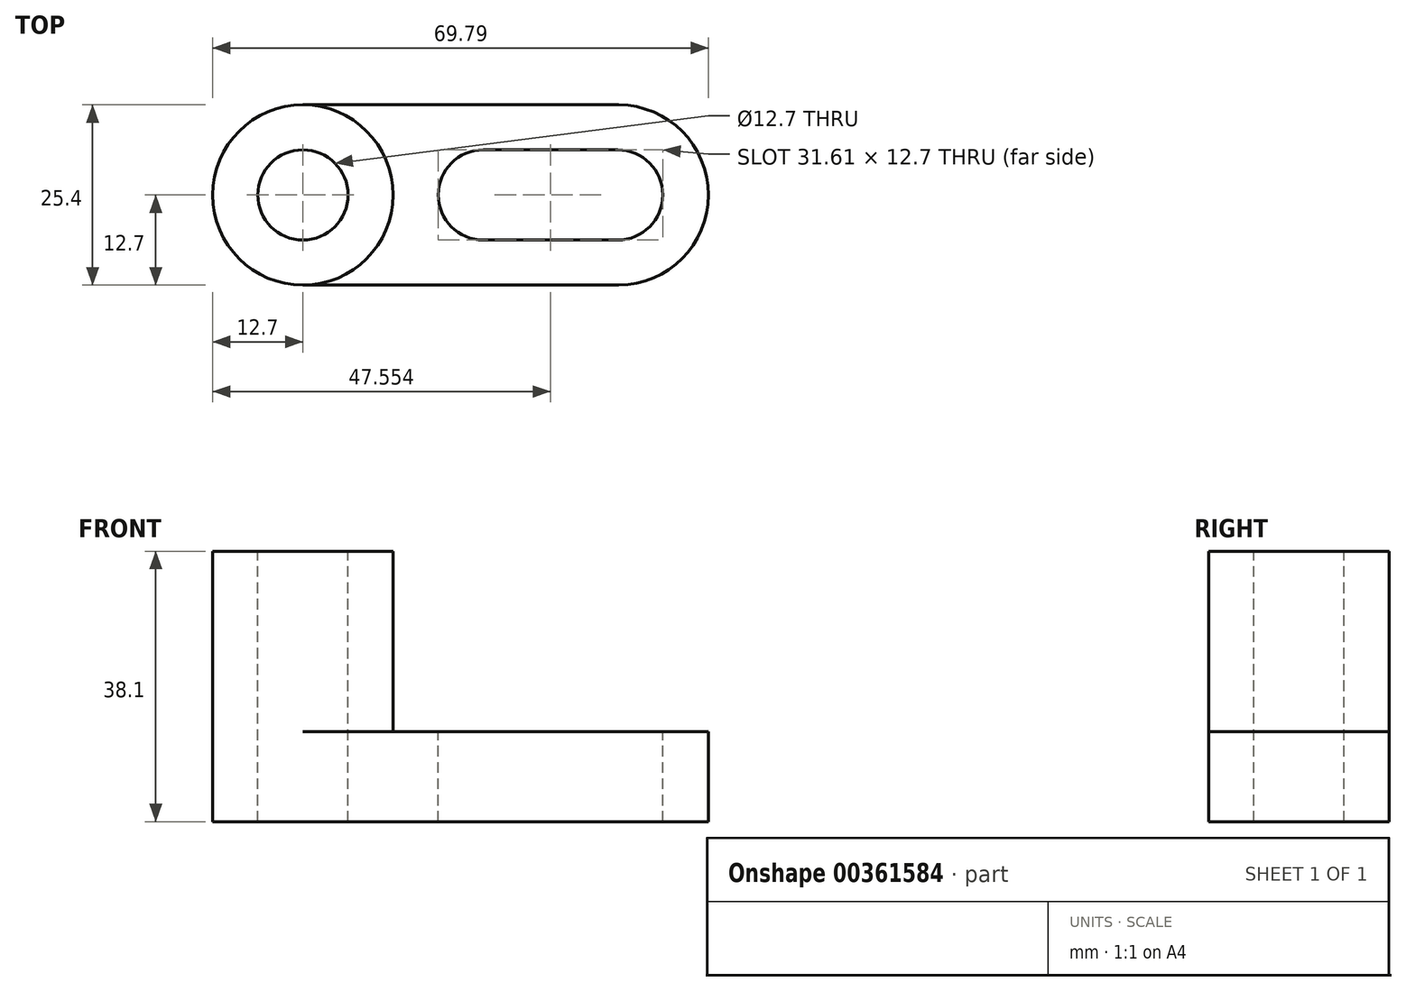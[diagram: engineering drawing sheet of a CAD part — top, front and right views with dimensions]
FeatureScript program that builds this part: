
annotation { "Feature Type Name" : "Feature", "Feature Type Description" : "" }
export const myFeature = defineFeature(function(context is Context, id is Id, definition is map)
    precondition{}
    {
        {
            var Q0;
            Q0=qCreatedBy(makeId("Front.planeOp"),FACE);
            var sketch = newSketch(context, id + "F0", { "sketchPlane" : qUnion([Q0])});
            skLineSegment(sketch, "E0", {"start": v(0, 0) * mm, "end": v(69.85, 0) * mm});
            skLineSegment(sketch, "E1", {"start": v(69.85, 0) * mm, "end": v(69.85, 12.7) * mm});
            skLineSegment(sketch, "E2", {"start": v(69.85, 12.7) * mm, "end": v(25.4, 12.7) * mm});
            skLineSegment(sketch, "E3", {"start": v(25.4, 12.7) * mm, "end": v(25.4, 38.1) * mm});
            skLineSegment(sketch, "E4", {"start": v(25.4, 38.1) * mm, "end": v(0, 38.1) * mm});
            skLineSegment(sketch, "E5", {"start": v(0, 38.1) * mm, "end": v(0, 0) * mm});
            skSolve(sketch);
        }
        {
            var Q0;
            Q0=makeQuery(id+"F0.imprint","IMPRINT",FACE,{"disambiguationData":[TD([[makeQuery(id+"F0.imprint","IMPRINT",EDGE,{"derivedFrom":sQuery(id+"F0.wireOp",EDGE,"E0")}),1.0]])]});
            extrude(context, id + "F1", {"entities" : qUnion([Q0]), "depth" : 25.4 * mm});
        }
        {
            var Q0;
            Q0=makeQuery(id+"F1.opExtrude","SWEPT_FACE",FACE,{"disambiguationData":[OSD([sQuery(id+"F0.wireOp",EDGE,"E4")])]});
            var sketch = newSketch(context, id + "F2", { "sketchPlane" : qUnion([Q0])});
            skCircle(sketch, "E6", {"center": v(12.7, -12.7) * mm, "radius": 12.7 * mm});
            skPoint(sketch, "E6.centerSnap0", {"position": v(25.4, -12.7) * mm});
            skSolve(sketch);
        }
        {
            var Q0;
            {var subQ0=sQuery(id+"F2.wireOp",EDGE,"E6");var subQ1=sQuery(id+"F0.wireOp",EDGE,"E4");var subQ2=makeQuery(id+"F1.opExtrude","CAP_EDGE",EDGE,{"disambiguationData":[OSD([subQ1])],"isStart":true});var subQ3=makeQuery(id+"F2.imprint","INTERSECT",VERTEX,{"derivedFrom":[subQ2,subQ0]});Q0=makeQuery(id+"F2.imprint","IMPRINT",FACE,{"disambiguationData":[TD([[makeQuery(id+"F2.imprint","IMPRINT",EDGE,{"disambiguationData":[TD([[subQ3,-1.0]])],"derivedFrom":subQ0}),-1.0]])]});}
            var Q1;
            {var subQ0=sQuery(id+"F2.wireOp",EDGE,"E6");var subQ1=sQuery(id+"F0.wireOp",EDGE,"E4");var subQ4=makeQuery(id+"F1.opExtrude","CAP_EDGE",EDGE,{"disambiguationData":[OSD([subQ1])],"isStart":false});var subQ5=makeQuery(id+"F2.imprint","INTERSECT",VERTEX,{"derivedFrom":[subQ4,subQ0]});Q1=makeQuery(id+"F2.imprint","IMPRINT",FACE,{"disambiguationData":[TD([[makeQuery(id+"F2.imprint","IMPRINT",EDGE,{"disambiguationData":[TD([[subQ5,1.0]])],"derivedFrom":subQ0}),-1.0]])]});}
            extrude(context, id + "F3", {"entities" : qUnion([Q0, Q1]), "operationType" : NewBodyOperationType.REMOVE, "oppositeDirection" : true, "depth" : 38.1 * mm});
        }
        {
            var Q0;
            Q0=makeQuery(id+"F1.opExtrude","SWEPT_FACE",FACE,{"disambiguationData":[OSD([sQuery(id+"F0.wireOp",EDGE,"E4")])]});
            var sketch = newSketch(context, id + "F4", { "sketchPlane" : qUnion([Q0])});
            skCircle(sketch, "E7", {"center": v(12.7, -12.7) * mm, "radius": 12.7 * mm});
            skSolve(sketch);
        }
        {
            var Q0;
            {var subQ1=sQuery(id+"F0.wireOp",EDGE,"E4");var subQ2=makeQuery(id+"F1.opExtrude","CAP_EDGE",EDGE,{"disambiguationData":[OSD([subQ1])],"isStart":true});Q0=makeQuery(id+"F4.imprint","IMPRINT",FACE,{"disambiguationData":[TD([[makeQuery(id+"F4.imprint","IMPRINT",EDGE,{"derivedFrom":subQ2}),1.0]])]});}
            var Q1;
            {var subQ1=sQuery(id+"F0.wireOp",EDGE,"E4");var subQ2=makeQuery(id+"F1.opExtrude","CAP_EDGE",EDGE,{"disambiguationData":[OSD([subQ1])],"isStart":false});Q1=makeQuery(id+"F4.imprint","IMPRINT",FACE,{"disambiguationData":[TD([[makeQuery(id+"F4.imprint","IMPRINT",EDGE,{"derivedFrom":subQ2}),-1.0]])]});}
            extrude(context, id + "F5", {"entities" : qUnion([Q0, Q1]), "operationType" : NewBodyOperationType.REMOVE, "oppositeDirection" : true, "depth" : 25.4 * mm});
        }
        {
            var Q0;
            Q0=makeQuery(id+"F1.opExtrude","SWEPT_FACE",FACE,{"disambiguationData":[OSD([sQuery(id+"F0.wireOp",EDGE,"E4")])]});
            var sketch = newSketch(context, id + "F6", { "sketchPlane" : qUnion([Q0])});
            skCircle(sketch, "E8", {"center": v(12.7, -12.7) * mm, "radius": 6.35 * mm});
            skSolve(sketch);
        }
        {
            var Q0;
            Q0=makeQuery(id+"F6.imprint","IMPRINT",FACE,{"disambiguationData":[TD([[makeQuery(id+"F6.imprint","IMPRINT",EDGE,{"derivedFrom":sQuery(id+"F6.wireOp",EDGE,"E8")}),1.0]])]});
            extrude(context, id + "F7", {"entities" : qUnion([Q0]), "operationType" : NewBodyOperationType.REMOVE, "oppositeDirection" : true, "depth" : 38.1 * mm});
        }
        {
            var Q0;
            {var subQ0=sQuery(id+"F0.wireOp",EDGE,"E4");var subQ1=makeQuery(id+"F1.opExtrude","CAP_EDGE",EDGE,{"disambiguationData":[OSD([subQ0])],"isStart":false});var subQ2=sQuery(id+"F0.wireOp",EDGE,"E3");var subQ3=makeQuery(id+"F1.opExtrude","SWEPT_EDGE",EDGE,{"disambiguationData":[OSD([subQ2,subQ0])]});var subQ4=sQuery(id+"F4.wireOp",EDGE,"E7");var subQ6=makeQuery(id+"F1.opExtrude","CAP_EDGE",EDGE,{"disambiguationData":[OSD([subQ0])],"isStart":true});Q0=makeQuery(id+"F5.boolean.opBoolean","MERGE",FACE,{"derivedFrom":[makeQuery(id+"F1.opExtrude","SWEPT_FACE",FACE,{"disambiguationData":[OSD([sQuery(id+"F0.wireOp",EDGE,"E2")])]}),makeQuery(id+"F5.opExtrude","CAP_FACE",FACE,{"disambiguationData":[OSD([subQ2,subQ0,subQ4]),TDD([makeQuery(id+"F4.imprint","IMPRINT",EDGE,{"disambiguationData":[TD([[makeQuery(id+"F4.imprint","INTERSECT",VERTEX,{"derivedFrom":[subQ6,subQ4]}),1.0]])],"derivedFrom":subQ4}),makeQuery(id+"F4.imprint","IMPRINT",EDGE,{"derivedFrom":subQ6}),makeQuery(id+"F4.imprint","IMPRINT",EDGE,{"disambiguationData":[TD([[makeQuery(id+"F4.imprint","INTERSECT",VERTEX,{"derivedFrom":[subQ3,subQ6]}),1.0]])],"derivedFrom":subQ3})])],"isStart":false}),makeQuery(id+"F5.opExtrude","CAP_FACE",FACE,{"disambiguationData":[OSD([subQ2,subQ0,subQ4]),TDD([makeQuery(id+"F4.imprint","IMPRINT",EDGE,{"disambiguationData":[TD([[makeQuery(id+"F4.imprint","INTERSECT",VERTEX,{"derivedFrom":[subQ1,subQ4]}),-1.0]])],"derivedFrom":subQ4}),makeQuery(id+"F4.imprint","IMPRINT",EDGE,{"derivedFrom":subQ1}),makeQuery(id+"F4.imprint","IMPRINT",EDGE,{"disambiguationData":[TD([[makeQuery(id+"F4.imprint","INTERSECT",VERTEX,{"derivedFrom":[subQ3,subQ1]}),-1.0]])],"derivedFrom":subQ3})])],"isStart":false})]});}
            var sketch = newSketch(context, id + "F8", { "sketchPlane" : qUnion([Q0])});
            skCircle(sketch, "E9", {"center": v(57, -12.7) * mm, "radius": 6.35 * mm});
            skCircle(sketch, "E10", {"center": v(38.1, -12.7) * mm, "radius": 6.35 * mm});
            skLineSegment(sketch, "E11", {"start": v(38.1, -6.35) * mm, "end": v(57, -6.35) * mm});
            skLineSegment(sketch, "E12", {"start": v(38.1, -19.05) * mm, "end": v(57, -19.05) * mm});
            skSolve(sketch);
        }
        {
            var Q0;
            {var subQ0=sQuery(id+"F8.wireOp",EDGE,"E10");var subQ1=makeQuery(id+"F8.imprint","INTERSECT",VERTEX,{"derivedFrom":[subQ0,sQuery(id+"F8.wireOp",EDGE,"E11")]});Q0=makeQuery(id+"F8.imprint","IMPRINT",FACE,{"disambiguationData":[TD([[makeQuery(id+"F8.imprint","IMPRINT",EDGE,{"disambiguationData":[TD([[subQ1,-1.0]])],"derivedFrom":subQ0}),1.0]])]});}
            var Q1;
            {var subQ0=sQuery(id+"F8.wireOp",EDGE,"E11");Q1=makeQuery(id+"F8.imprint","IMPRINT",FACE,{"disambiguationData":[TD([[makeQuery(id+"F8.imprint","IMPRINT",EDGE,{"derivedFrom":subQ0}),-1.0]])]});}
            var Q2;
            {var subQ0=sQuery(id+"F8.wireOp",EDGE,"E9");var subQ1=makeQuery(id+"F8.imprint","INTERSECT",VERTEX,{"derivedFrom":[subQ0,sQuery(id+"F8.wireOp",EDGE,"E11")]});Q2=makeQuery(id+"F8.imprint","IMPRINT",FACE,{"disambiguationData":[TD([[makeQuery(id+"F8.imprint","IMPRINT",EDGE,{"disambiguationData":[TD([[subQ1,-1.0]])],"derivedFrom":subQ0}),1.0]])]});}
            extrude(context, id + "F9", {"entities" : qUnion([Q0, Q1, Q2]), "operationType" : NewBodyOperationType.REMOVE, "oppositeDirection" : true, "depth" : 12.7 * mm});
        }
        {
            var Q0;
            {var subQ0=sQuery(id+"F0.wireOp",EDGE,"E4");var subQ1=makeQuery(id+"F1.opExtrude","CAP_EDGE",EDGE,{"disambiguationData":[OSD([subQ0])],"isStart":false});var subQ2=sQuery(id+"F0.wireOp",EDGE,"E3");var subQ3=makeQuery(id+"F1.opExtrude","SWEPT_EDGE",EDGE,{"disambiguationData":[OSD([subQ2,subQ0])]});var subQ4=sQuery(id+"F4.wireOp",EDGE,"E7");var subQ6=makeQuery(id+"F1.opExtrude","CAP_EDGE",EDGE,{"disambiguationData":[OSD([subQ0])],"isStart":true});Q0=makeQuery(id+"F5.boolean.opBoolean","MERGE",FACE,{"derivedFrom":[makeQuery(id+"F1.opExtrude","SWEPT_FACE",FACE,{"disambiguationData":[OSD([sQuery(id+"F0.wireOp",EDGE,"E2")])]}),makeQuery(id+"F5.opExtrude","CAP_FACE",FACE,{"disambiguationData":[OSD([subQ2,subQ0,subQ4]),TDD([makeQuery(id+"F4.imprint","IMPRINT",EDGE,{"disambiguationData":[TD([[makeQuery(id+"F4.imprint","INTERSECT",VERTEX,{"derivedFrom":[subQ6,subQ4]}),1.0]])],"derivedFrom":subQ4}),makeQuery(id+"F4.imprint","IMPRINT",EDGE,{"derivedFrom":subQ6}),makeQuery(id+"F4.imprint","IMPRINT",EDGE,{"disambiguationData":[TD([[makeQuery(id+"F4.imprint","INTERSECT",VERTEX,{"derivedFrom":[subQ3,subQ6]}),1.0]])],"derivedFrom":subQ3})])],"isStart":false}),makeQuery(id+"F5.opExtrude","CAP_FACE",FACE,{"disambiguationData":[OSD([subQ2,subQ0,subQ4]),TDD([makeQuery(id+"F4.imprint","IMPRINT",EDGE,{"disambiguationData":[TD([[makeQuery(id+"F4.imprint","INTERSECT",VERTEX,{"derivedFrom":[subQ1,subQ4]}),-1.0]])],"derivedFrom":subQ4}),makeQuery(id+"F4.imprint","IMPRINT",EDGE,{"derivedFrom":subQ1}),makeQuery(id+"F4.imprint","IMPRINT",EDGE,{"disambiguationData":[TD([[makeQuery(id+"F4.imprint","INTERSECT",VERTEX,{"derivedFrom":[subQ3,subQ1]}),-1.0]])],"derivedFrom":subQ3})])],"isStart":false})]});}
            var sketch = newSketch(context, id + "F10", { "sketchPlane" : qUnion([Q0])});
            skArc(sketch, "E13", {"start": v(57, -25.4) * mm, "mid": v(69.79, -12.7) * mm, "end": v(57, 0) * mm});
            skSolve(sketch);
        }
        {
            var Q0;
            {var subQ2=sQuery(id+"F0.wireOp",EDGE,"E2");var subQ7=makeQuery(id+"F1.opExtrude","SWEPT_EDGE",EDGE,{"disambiguationData":[OSD([sQuery(id+"F0.wireOp",EDGE,"E1"),subQ2])]});Q0=makeQuery(id+"F10.imprint","IMPRINT",FACE,{"disambiguationData":[TD([[makeQuery(id+"F10.imprint","IMPRINT",EDGE,{"derivedFrom":subQ7}),1.0]])]});}
            extrude(context, id + "F11", {"entities" : qUnion([Q0]), "operationType" : NewBodyOperationType.REMOVE, "oppositeDirection" : true, "depth" : 12.7 * mm});
        }
    });
